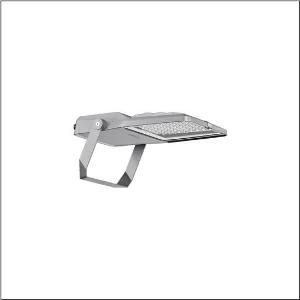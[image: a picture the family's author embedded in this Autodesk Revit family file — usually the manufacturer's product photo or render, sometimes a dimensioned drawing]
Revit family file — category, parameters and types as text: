
# Revit family: floodlight_fl_21_mini___pl52_5xa7776d2d1a_6cb1
name_source: partatom
category: Lighting Fixtures
units: mm (PartAtom-declared; Revit-internal decimal feet)

## family parameters
Cut with Voids When Loaded = No
Host = Face
Light Source = No
Part Type = Normal
Room Calculation Point = No
Round Connector Dimension = Use Diameter
Shared = No

## types (1)
- --- (1 x LED, 17840 lm, 142.9 W, 3000K)
    Apparent Load = 143 VA
    CIE Flux Codes = 26 60 98 100 100
    Color Rendering = 70
    Color Temperature = 3000K
    Default Elevation = 1800 mm
    Description = Floodlight FL 21 mini, floodlight, primary light control with lens, of PMMA, primary optical cover: protective disc, of toughened safety glass, transparent, light distribution: PL52, light emission: direct distribution, installation type: surface-mounted, LED, High Power LED, rated luminous flux: 17.840lm, luminous efficacy: 125lm/W, light colour: 730, colour temperature: 3000K, control: flexible luminous flux parameterisation, time-dependent luminous flux control, constant luminous flux control, overheat protection, presetting dimming logarithmic, with terminal, 6-pole, mains connection: 220..240V, AC, 50/60Hz, start of lifetime: 143W, end of service life: 151W, reduction: 63W, luminaire housing, of diecast aluminium, powder-coated, Siteco® metallic grey (DB 702S), corrosivity category C5 mid according to DIN EN ISO 12944, sealing non-destructively replaceable, mounting bracket, of steel, galvanised, powder-coated, Siteco® metallic grey (DB 702S), Smart Interface below and above, protection rating (complete): IP66, insulation class (complete): insulation class II (safety insulation), certification: CE, ENEC, VDE, protection symbol: D, impact resistance: IK08, permissible operating ambient temperature: -40..+40°C, permissible operating ambient temperature for outdoor applications: -40..+50°C, standard: DIN EN 12944, LABS conformity tested according to VDMA 24364:2018-05, packaging unit: 1 piece

Light Distribution: PL52
    Height = 70 mm
    Lamp = 1 x LED
    Lamp Light Flux = 17840 lm
    Lamp Power = 142.9 W
    Lamp count = 1
    Length = 485 mm
    Luminous efficacy = 125 lm/W
    Manufacturer = Siteco
    ModVariant = No
    Model = 5XA7776D2D1A
    Number of Poles = 1
    OnlyDefault = Yes
    Power Factor = 1
    Product Name = Floodlight FL 21 mini | PL52
    Product group = floodlight | pylon annexe
    ProductGroupID = 6200
    Protection Class = Protection class II
    Protection Degree = IP 66
    RLX_Detail_Level = 1
    RLX_Emergency_Light_Flux = 0 lm
    RLX_Emergency_Type = 0
    RLX_Emergency_Type_DB = No
    RlxData = <blob elided: 96497 chars, md5=aed45fab>
    Socket = socket
    Standby Power = 0 W
    System Light Flux = 17840 lm
    System Power = 143 W
    Type Comments = factory setting: luminous flux: 100 % | dim-lin: 254 | 730 mA
    Type Image = l_1006845.jpg
    URL = http://relux.com
    VarID = @adj_095449
    Voltage = 0 V
    Weight = 0.00 kg
    Width = 337 mm

## geometry (parser evidence)
native form markers: Blend x4, Sweep x14
no freeform markers — native parametric forms only
